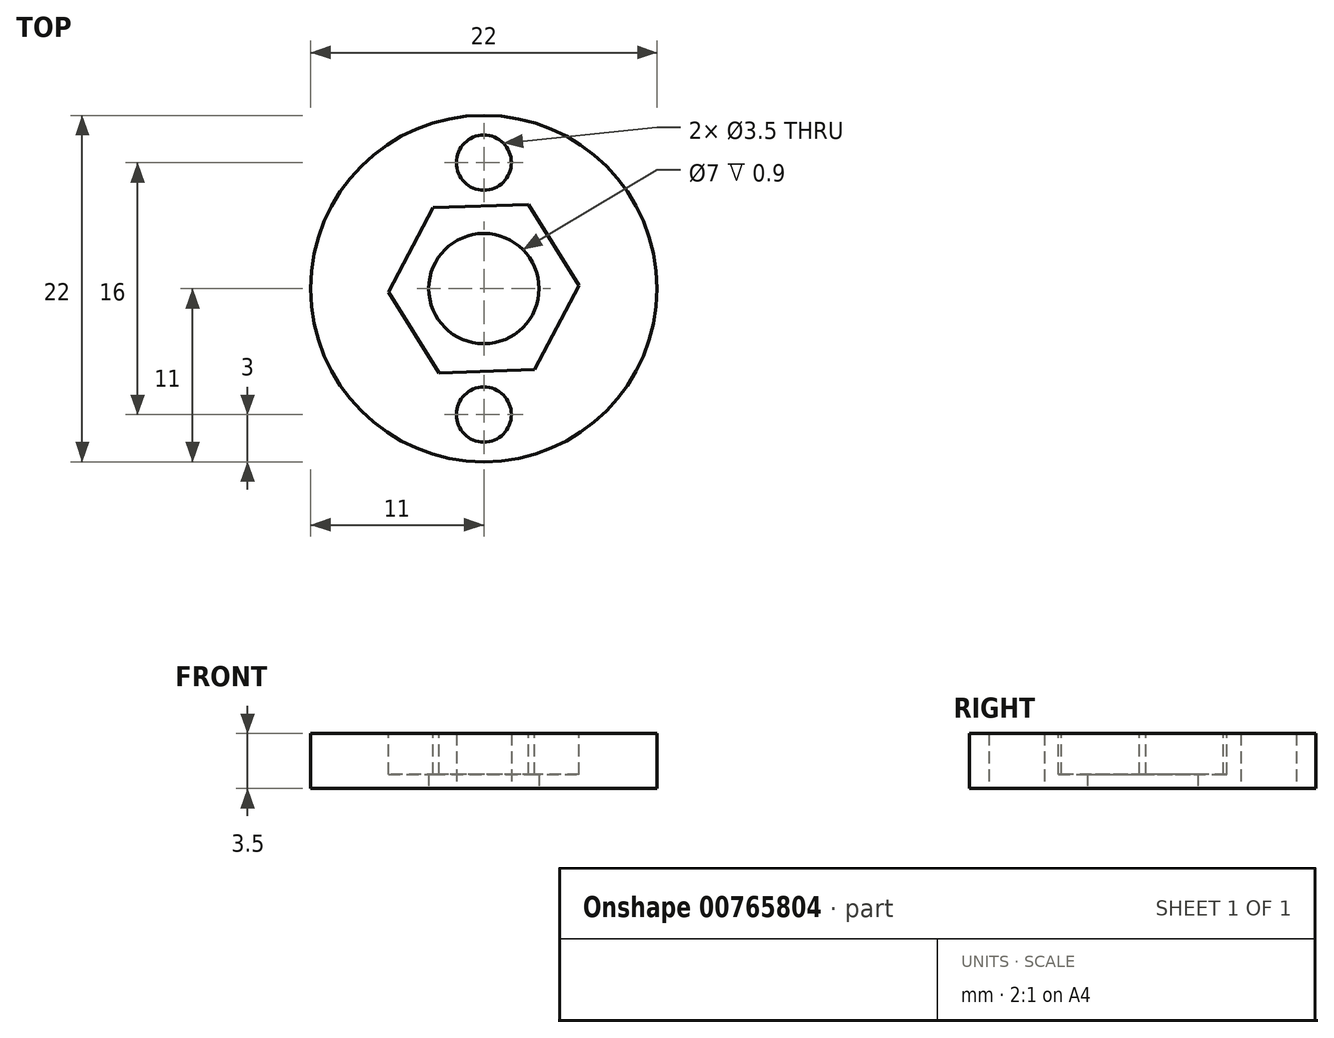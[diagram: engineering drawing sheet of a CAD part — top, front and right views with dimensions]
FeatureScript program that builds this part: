
annotation { "Feature Type Name" : "Feature", "Feature Type Description" : "" }
export const myFeature = defineFeature(function(context is Context, id is Id, definition is map)
    precondition{}
    {
        {
            var Q0;
            Q0=qCreatedBy(makeId("Top.planeOp"),FACE);
            var sketch = newSketch(context, id + "F0", { "sketchPlane" : qUnion([Q0])});
            skCircle(sketch, "E0", {"center": v(0, 0) * mm, "radius": 11 * mm});
            skCircle(sketch, "E1", {"center": v(0, 8) * mm, "radius": 1.75 * mm});
            skCircle(sketch, "E2.1.0", {"center": v(0, -8) * mm, "radius": 1.75 * mm});
            skCircle(sketch, "E3.cCircle", {"center": v(0, 0) * mm, "radius": 5.25 * mm, "construction": true});
            skLineSegment(sketch, "E3.0", {"start": v(-6.06, -0.2) * mm, "end": v(-3.21, 5.14) * mm});
            skLineSegment(sketch, "E3.1", {"start": v(-3.21, 5.14) * mm, "end": v(2.85, 5.35) * mm});
            skLineSegment(sketch, "E3.2", {"start": v(2.85, 5.35) * mm, "end": v(6.06, 0.2) * mm});
            skLineSegment(sketch, "E3.3", {"start": v(6.06, 0.2) * mm, "end": v(3.21, -5.14) * mm});
            skLineSegment(sketch, "E3.4", {"start": v(3.21, -5.14) * mm, "end": v(-2.85, -5.35) * mm});
            skLineSegment(sketch, "E3.5", {"start": v(-2.85, -5.35) * mm, "end": v(-6.06, -0.2) * mm});
            skPoint(sketch, "E3.0.midPoint", {"position": v(-4.63, 2.47) * mm});
            skCircle(sketch, "E4", {"center": v(0, 0) * mm, "radius": 3.5 * mm});
            skSolve(sketch);
        }
        {
            var Q0;
            Q0=makeQuery(id+"F0.imprint","IMPRINT",FACE,{"disambiguationData":[TD([[makeQuery(id+"F0.imprint","IMPRINT",EDGE,{"derivedFrom":sQuery(id+"F0.wireOp",EDGE,"E0")}),1.0]])]});
            var Q1;
            Q1=makeQuery(id+"F0.imprint","IMPRINT",FACE,{"disambiguationData":[TD([[makeQuery(id+"F0.imprint","IMPRINT",EDGE,{"derivedFrom":sQuery(id+"F0.wireOp",EDGE,"E3.0")}),-1.0]])]});
            extrude(context, id + "F1", {"entities" : qUnion([Q0, Q1]), "endBound" : BoundingType.SYMMETRIC, "depth" : 7 * mm, "offsetDistance" : 25 * mm});
        }
        {
            var Q0;
            Q0=makeQuery(id+"F0.imprint","IMPRINT",FACE,{"disambiguationData":[TD([[makeQuery(id+"F0.imprint","IMPRINT",EDGE,{"derivedFrom":sQuery(id+"F0.wireOp",EDGE,"E3.0")}),-1.0]])]});
            extrude(context, id + "F2", {"entities" : qUnion([Q0]), "operationType" : NewBodyOperationType.REMOVE, "endBound" : BoundingType.SYMMETRIC, "oppositeDirection" : true, "depth" : 5.2 * mm, "offsetDistance" : 25 * mm});
        }
        {
            var Q0;
            Q0=qCreatedBy(makeId("Top.planeOp"),FACE);
            var sketch = newSketch(context, id + "F3", { "sketchPlane" : qUnion([Q0])});
            skLineSegment(sketch, "E5.bottom", {"start": v(-11, 11) * mm, "end": v(11, 11) * mm});
            skLineSegment(sketch, "E5.top", {"start": v(-11, -11) * mm, "end": v(11, -11) * mm});
            skLineSegment(sketch, "E5.left", {"start": v(-11, 11) * mm, "end": v(-11, -11) * mm});
            skLineSegment(sketch, "E5.right", {"start": v(11, 11) * mm, "end": v(11, -11) * mm});
            skSolve(sketch);
        }
        {
            var Q0;
            Q0 = qSketchRegion(id + "F3", true);
            extrude(context, id + "F4", {"entities" : qUnion([Q0]), "operationType" : NewBodyOperationType.REMOVE, "depth" : 25 * mm, "offsetDistance" : 25 * mm});
        }
    });
